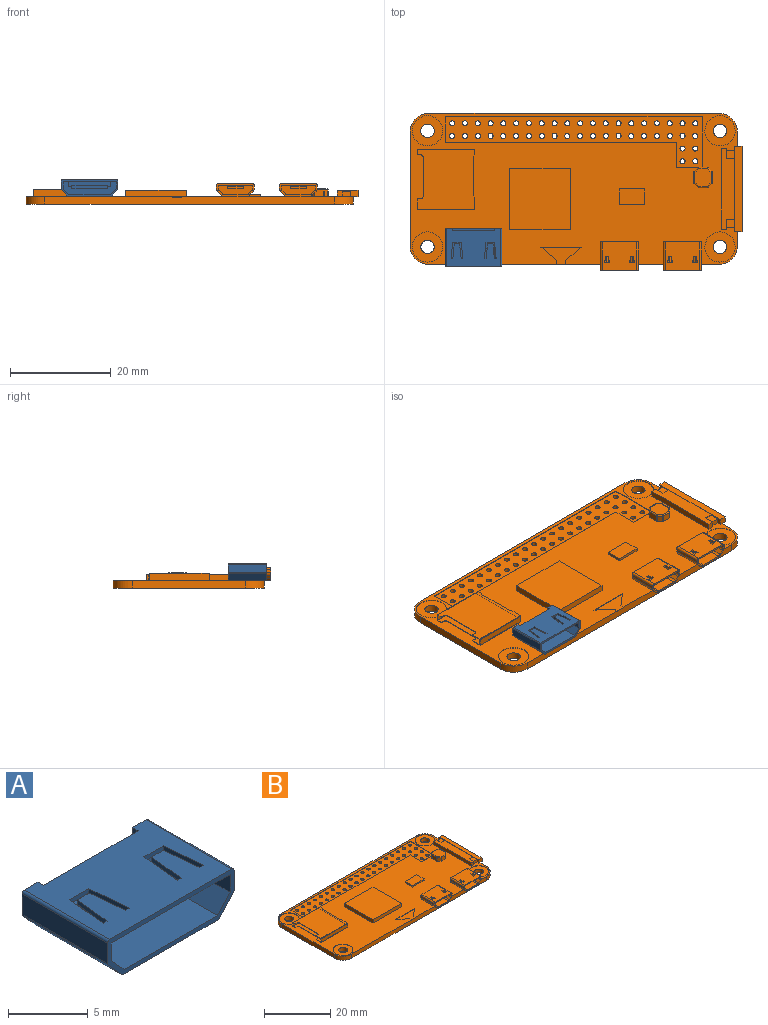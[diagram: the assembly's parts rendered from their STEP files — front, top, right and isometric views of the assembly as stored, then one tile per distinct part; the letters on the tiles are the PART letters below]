
ASSEMBLY  parts=2 mates=1
PART A: 46 faces, bbox 11.3x7.6x3.3 mm
  f0: plane 10.55x2.6mm, normal (0,-1,0), area 22.2mm2, adj f15,f16,f17,f18,f19,f20,f21,f22
  f1: plane 7.6x1.57mm, normal (-1,0,0), area 12mm2, adj f7,f8,f11,f13
  f2: plane 10.85x7.6mm, normal (0,0,1), area 72.9mm2, adj f7,f8,f13,f14,f26,f27,f28,f29
  f3: plane 7.6x1.57mm, normal (1,0,0), area 12mm2, adj f7,f8,f12,f14
  f4: plane 7.6x1.33mm, normal (0.74,0,-0.67), area 13.7mm2, adj f7,f8,f9,f12
  f5: plane 8.42x7.6mm, normal (0,0,-1), area 64mm2, adj f7,f8,f9,f10
  f6: plane 7.6x1.33mm, normal (-0.74,0,-0.67), area 13.7mm2, adj f7,f8,f10,f11
  f7: plane 11.25x3.3mm, normal (0,1,0), area 23.4mm2, adj f1,f2,f3,f4,f5,f6,f9,f10
  f8: plane 11.25x3.3mm, normal (0,-1,0), area 9.1mm2, adj f1,f2,f3,f4,f5,f6,f9,f10
  f9: cylinder r=0.2mm len=7.6mm, axis (0,-1,0), area 1.3mm2, adj f4,f5,f7,f8
  f10: cylinder r=0.2mm len=7.6mm, axis (0,-1,0), area 1.3mm2, adj f5,f6,f7,f8
  f11: cylinder r=0.2mm len=7.6mm, axis (0,-1,0), area 1.1mm2, adj f1,f6,f7,f8
  f12: cylinder r=0.2mm len=7.6mm, axis (0,-1,0), area 1.1mm2, adj f3,f4,f7,f8
  f13: cylinder r=0.2mm len=7.6mm, axis (0,-1,0), area 2.4mm2, adj f1,f2,f7,f8
  f14: cylinder r=0.2mm len=7.6mm, axis (0,-1,0), area 2.4mm2, adj f2,f3,f7,f8
  f15: plane 10.55x7mm, normal (0,0,-1), area 68.5mm2, adj f0,f8,f16,f20,f26,f27,f28,f29
  f16: plane 7x1.36mm, normal (-1,0,0), area 9.5mm2, adj f0,f8,f15,f17
  f17: plane 7x1.24mm, normal (-0.74,0,0.67), area 11.7mm2, adj f0,f8,f16,f18
  f18: plane 8.29x7mm, normal (0,0,1), area 58mm2, adj f0,f8,f17,f19
  f19: plane 7x1.24mm, normal (0.74,0,0.67), area 11.7mm2, adj f0,f8,f18,f20
  f20: plane 7x1.36mm, normal (1,0,0), area 9.5mm2, adj f0,f8,f15,f19
  f21: plane 3.5x0.55mm, normal (-1,0,0), area 1.9mm2, adj f0,f22,f24,f25
  f22: plane 7x3.5mm, normal (0,0,-1), area 24.5mm2, adj f0,f21,f23,f25
  f23: plane 3.5x0.55mm, normal (1,0,0), area 1.9mm2, adj f0,f22,f24,f25
  f24: plane 7x3.5mm, normal (0,0,1), area 24.5mm2, adj f0,f21,f23,f25
  f25: plane 7x0.55mm, normal (0,-1,0), area 3.8mm2, adj f21,f22,f23,f24
  f26: plane 3.3x0.35mm, normal (-1,-0.1,0), area 1.2mm2, adj f2,f15,f27,f33
  f27: plane 1.7x0.35mm, normal (0,-1,0), area 0.6mm2, adj f2,f15,f26,f28
  f28: plane 3.3x0.35mm, normal (1,-0.1,0), area 1.2mm2, adj f2,f15,f27,f29
  f29: plane 0.35x0.35mm, normal (0,1,0), area 0.1mm2, adj f2,f15,f28,f30
  f30: plane 2.95x0.35mm, normal (-1,0.1,0), area 1mm2, adj f2,f15,f29,f31
  f31: plane 1.07x0.35mm, normal (0,1,0), area 0.4mm2, adj f2,f15,f30,f32
  f32: plane 2.95x0.35mm, normal (1,0.1,0), area 1mm2, adj f2,f15,f31,f33
  f33: plane 0.35x0.35mm, normal (0,1,0), area 0.1mm2, adj f2,f15,f26,f32
  f34: plane 1.7x0.35mm, normal (0,-1,0), area 0.6mm2, adj f2,f15,f35,f41
  f35: plane 3.3x0.35mm, normal (1,-0.1,0), area 1.2mm2, adj f2,f15,f34,f36
  f36: plane 0.35x0.35mm, normal (0,1,0), area 0.1mm2, adj f2,f15,f35,f37
  f37: plane 2.95x0.35mm, normal (-1,0.1,0), area 1mm2, adj f2,f15,f36,f38
  f38: plane 1.07x0.35mm, normal (0,1,0), area 0.4mm2, adj f2,f15,f37,f39
  f39: plane 2.95x0.35mm, normal (1,0.1,0), area 1mm2, adj f2,f15,f38,f40
  f40: plane 0.35x0.35mm, normal (0,1,0), area 0.1mm2, adj f2,f15,f39,f41
  f41: plane 3.3x0.35mm, normal (-1,-0.1,0), area 1.2mm2, adj f2,f15,f34,f40
  f42: plane 1.4x0.5mm, normal (-1,0,0), area 0.7mm2, adj f2,f7,f44,f45
  f43: plane 1.4x0.5mm, normal (1,0,0), area 0.7mm2, adj f2,f7,f44,f45
  f44: plane 8.4x0.5mm, normal (0,0,1), area 4.2mm2, adj f7,f42,f43,f45
  f45: plane 8.4x1.4mm, normal (0,1,0), area 11.8mm2, adj f2,f42,f43,f44
PART B: 270 faces, bbox 65.9x31.3x4.1 mm
  f0: cylinder r=3mm len=6mm, axis (0,0,1), area 1.9mm2, adj f52,f91
  f1: cylinder r=3mm len=6mm, axis (0,0,1), area 1.9mm2, adj f52,f90
  f2: cylinder r=3mm len=6mm, axis (0,0,1), area 1.9mm2, adj f52,f89
  f3: cylinder r=3mm len=6mm, axis (0,0,1), area 1.9mm2, adj f52,f81
  f4: cylinder r=1.32mm len=2.65mm, axis (0,0,1), area 11.7mm2, adj f80,f81
  f5: cylinder r=0.5mm len=1.4mm, axis (0,0,1), area 4.4mm2, adj f80,f82
  f6: cylinder r=0.5mm len=1.4mm, axis (0,0,1), area 4.4mm2, adj f80,f82
  f7: cylinder r=0.5mm len=1.4mm, axis (0,0,1), area 4.4mm2, adj f80,f82
  f8: cylinder r=0.5mm len=1.4mm, axis (0,0,1), area 4.4mm2, adj f80,f82
  f9: cylinder r=0.5mm len=1.4mm, axis (0,0,1), area 4.4mm2, adj f80,f82
  f10: cylinder r=0.5mm len=1.4mm, axis (0,0,1), area 4.4mm2, adj f80,f82
  f11: cylinder r=0.5mm len=1.4mm, axis (0,0,1), area 4.4mm2, adj f80,f82
  f12: cylinder r=0.5mm len=1.4mm, axis (0,0,1), area 4.4mm2, adj f80,f82
  f13: cylinder r=1.32mm len=2.65mm, axis (0,0,1), area 11.7mm2, adj f80,f89
  f14: cylinder r=1.32mm len=2.65mm, axis (0,0,1), area 11.7mm2, adj f80,f90
  f15: cylinder r=1.32mm len=2.65mm, axis (0,0,1), area 11.7mm2, adj f80,f91
  f16: cylinder r=0.5mm len=1.4mm, axis (0,0,1), area 4.4mm2, adj f80,f82
  f17: cylinder r=0.5mm len=1.4mm, axis (0,0,1), area 4.4mm2, adj f80,f82
  f18: cylinder r=0.5mm len=1.4mm, axis (0,0,1), area 4.4mm2, adj f80,f82
  f19: cylinder r=0.5mm len=1.4mm, axis (0,0,1), area 4.4mm2, adj f80,f82
  f20: cylinder r=0.5mm len=1.4mm, axis (0,0,1), area 4.4mm2, adj f80,f82
  f21: cylinder r=0.5mm len=1.4mm, axis (0,0,1), area 4.4mm2, adj f80,f82
  f22: cylinder r=0.5mm len=1.4mm, axis (0,0,1), area 4.4mm2, adj f80,f82
  f23: cylinder r=0.5mm len=1.4mm, axis (0,0,1), area 4.4mm2, adj f80,f82
  f24: cylinder r=0.5mm len=1.4mm, axis (0,0,1), area 4.4mm2, adj f80,f82
  f25: cylinder r=0.5mm len=1.4mm, axis (0,0,1), area 4.4mm2, adj f80,f82
  f26: cylinder r=0.5mm len=1.4mm, axis (0,0,1), area 4.4mm2, adj f80,f82
  f27: cylinder r=0.5mm len=1.4mm, axis (0,0,1), area 4.4mm2, adj f80,f82
  f28: cylinder r=0.5mm len=1.4mm, axis (0,0,1), area 4.4mm2, adj f80,f82
  f29: cylinder r=0.5mm len=1.4mm, axis (0,0,1), area 4.4mm2, adj f80,f82
  f30: cylinder r=0.5mm len=1.4mm, axis (0,0,1), area 4.4mm2, adj f80,f82
  f31: cylinder r=0.5mm len=1.4mm, axis (0,0,1), area 4.4mm2, adj f80,f82
  f32: cylinder r=0.5mm len=1.4mm, axis (0,0,1), area 4.4mm2, adj f80,f82
  f33: cylinder r=0.5mm len=1.4mm, axis (0,0,1), area 4.4mm2, adj f80,f82
  f34: cylinder r=0.5mm len=1.4mm, axis (0,0,1), area 4.4mm2, adj f80,f82
  f35: cylinder r=0.5mm len=1.4mm, axis (0,0,1), area 4.4mm2, adj f80,f82
  f36: cylinder r=0.5mm len=1.4mm, axis (0,0,1), area 4.4mm2, adj f80,f82
  f37: cylinder r=0.5mm len=1.4mm, axis (0,0,1), area 4.4mm2, adj f80,f82
  f38: cylinder r=0.5mm len=1.4mm, axis (0,0,1), area 4.4mm2, adj f80,f82
  f39: cylinder r=0.5mm len=1.4mm, axis (0,0,1), area 4.4mm2, adj f80,f82
  f40: cylinder r=0.5mm len=1.4mm, axis (0,0,1), area 4.4mm2, adj f80,f82
  f41: cylinder r=0.5mm len=1.4mm, axis (0,0,1), area 4.4mm2, adj f80,f82
  f42: cylinder r=0.5mm len=1.4mm, axis (0,0,1), area 4.4mm2, adj f80,f82
  f43: cylinder r=0.5mm len=1.4mm, axis (0,0,1), area 4.4mm2, adj f80,f82
  f44: cylinder r=0.5mm len=1.4mm, axis (0,0,1), area 4.4mm2, adj f80,f82
  f45: cylinder r=0.5mm len=1.4mm, axis (0,0,1), area 4.4mm2, adj f80,f82
  f46: cylinder r=0.5mm len=1.4mm, axis (0,0,1), area 4.4mm2, adj f80,f82
  f47: cylinder r=0.5mm len=1.4mm, axis (0,0,1), area 4.4mm2, adj f80,f82
  f48: cylinder r=0.5mm len=1.4mm, axis (0,0,1), area 4.4mm2, adj f80,f82
  f49: cylinder r=0.5mm len=1.4mm, axis (0,0,1), area 4.4mm2, adj f80,f82
  f50: cylinder r=0.5mm len=1.4mm, axis (0,0,1), area 4.4mm2, adj f80,f82
  f51: cylinder r=0.5mm len=1.4mm, axis (0,0,1), area 4.4mm2, adj f80,f82
  f52: plane 65x30mm, normal (0,0,1), area 1137.8mm2, adj f0,f1,f2,f3,f53,f54,f55,f60
  f53: plane 17x1.2mm, normal (-1,0,0), area 2.7mm2, adj f52,f56,f212,f213,f214,f221,f222,f227
  f54: plane 2x1.19mm, normal (1,0,0), area 0.7mm2, adj f52,f221,f222,f223,f229,f230
  f55: plane 2x1.19mm, normal (1,0,0), area 0.7mm2, adj f52,f56,f221,f225,f227,f228
  f56: plane 1.6x0.19mm, normal (0,1,0), area 0.3mm2, adj f53,f55,f221,f228
  f57: plane 11.9x0.5mm, normal (0,0,1), area 6mm2, adj f77,f216,f218,f226
  f58: plane 6.91x1.96mm, normal (0,-1,0), area 11.2mm2, adj f158,f159,f160,f161,f162,f163,f164,f165
  f59: plane 6.91x1.96mm, normal (0,-1,0), area 11.2mm2, adj f146,f147,f148,f149,f150,f151,f152,f153
  f60: plane 1.45x1.1mm, normal (-1,0,0), area 0.3mm2, adj f52,f61,f62,f109,f110,f111,f113,f114
  f61: plane 0.65x0.1mm, normal (0,-1,0), area 0.1mm2, adj f52,f60,f63,f114
  f62: plane 0.65x0.1mm, normal (0,-1,0), area 0.1mm2, adj f60,f64,f110,f116
  f63: cylinder r=0.5mm len=0.5mm, axis (0,0,-1), area 0.1mm2, adj f52,f61,f65,f114
  f64: cylinder r=0.5mm len=0.5mm, axis (0,0,-1), area 0.1mm2, adj f62,f66,f110,f116
  f65: plane 7.75x0.1mm, normal (-1,0,0), area 0.8mm2, adj f52,f63,f67,f114
  f66: plane 7.75x0.1mm, normal (-1,0,0), area 0.8mm2, adj f64,f68,f110,f116
  f67: cylinder r=0.5mm len=0.5mm, axis (0,0,-1), area 0.1mm2, adj f52,f65,f69,f114
  f68: cylinder r=0.5mm len=0.5mm, axis (0,0,-1), area 0.1mm2, adj f66,f70,f110,f116
  f69: plane 0.65x0.1mm, normal (0,1,0), area 0.1mm2, adj f52,f67,f71,f114
  f70: plane 0.65x0.1mm, normal (0,1,0), area 0.1mm2, adj f68,f71,f110,f116
  f71: plane 2.15x1.45mm, normal (-1,0,0), area 0.6mm2, adj f52,f69,f70,f103,f110,f112,f114,f115
  f72: cylinder r=3.75mm len=3.75mm, axis (0,0,-1), area 8.8mm2, adj f52,f73,f79,f80
  f73: plane 22.5x1.5mm, normal (-1,0,0), area 33.8mm2, adj f52,f72,f74,f80
  f74: cylinder r=3.75mm len=3.75mm, axis (0,0,-1), area 8.8mm2, adj f52,f73,f75,f80
  f75: plane 57.5x1.5mm, normal (0,-1,0), area 86.1mm2, adj f52,f74,f76,f80,f95,f96,f97,f118
  f76: cylinder r=3.75mm len=3.75mm, axis (0,0,-1), area 8.8mm2, adj f52,f75,f77,f80
  f77: plane 22.5x1.5mm, normal (1,0,0), area 33.8mm2, adj f52,f57,f76,f78,f80,f215,f219
  f78: cylinder r=3.75mm len=3.75mm, axis (0,0,-1), area 8.8mm2, adj f52,f77,f79,f80
  f79: plane 57.5x1.5mm, normal (0,1,0), area 86.3mm2, adj f52,f72,f78,f80
  f80: plane 65x30mm, normal (0,0,-1), area 1881.3mm2, adj f4,f5,f6,f7,f8,f9,f10,f11
  f81: plane 6x6mm, normal (0,0,1), area 22.8mm2, adj f3,f4
  f82: plane 51x10.1mm, normal (0,0,1), area 251mm2, adj f5,f6,f7,f8,f9,f10,f11,f12
  f83: plane 5.1x0.1mm, normal (1,0,0), area 0.5mm2, adj f52,f82,f84,f88
  f84: plane 51x0.1mm, normal (0,-1,0), area 5.1mm2, adj f52,f82,f83,f85
  f85: plane 10.1x0.1mm, normal (-1,0,0), area 1mm2, adj f52,f82,f84,f86,f231
  f86: plane 5.1x0.1mm, normal (0,1,0), area 0.5mm2, adj f52,f82,f85,f87,f231
  f87: plane 5x0.1mm, normal (1,0,0), area 0.5mm2, adj f52,f82,f86,f88
  f88: plane 45.9x0.1mm, normal (0,1,0), area 4.6mm2, adj f52,f82,f83,f87
  f89: plane 6x6mm, normal (0,0,1), area 22.8mm2, adj f2,f13
  f90: plane 6x6mm, normal (0,0,1), area 22.8mm2, adj f1,f14
  f91: plane 6x6mm, normal (0,0,1), area 22.8mm2, adj f0,f15
  f92: plane 3.08x2.65mm, normal (0.65,0.76,0), area 0.4mm2, adj f52,f93,f96,f97
  f93: plane 8x0.1mm, normal (0,-1,0), area 0.8mm2, adj f52,f92,f94,f97
  f94: plane 3.08x2.65mm, normal (-0.65,0.76,0), area 0.4mm2, adj f52,f93,f95,f97
  f95: plane 0.8x0.1mm, normal (-1,0,0), area 0.1mm2, adj f52,f75,f94,f97
  f96: plane 0.8x0.1mm, normal (1,0,0), area 0.1mm2, adj f52,f75,f92,f97
  f97: plane 8x3.45mm, normal (0,0,1), area 14.5mm2, adj f75,f92,f93,f94,f95,f96
  f98: plane 12x1.25mm, normal (1,0,0), area 15mm2, adj f52,f99,f101,f102
  f99: plane 12x1.25mm, normal (0,1,0), area 15mm2, adj f52,f98,f100,f102
  f100: plane 12x1.25mm, normal (-1,0,0), area 15mm2, adj f52,f99,f101,f102
  f101: plane 12x1.25mm, normal (0,-1,0), area 15mm2, adj f52,f98,f100,f102
  f102: plane 12x12mm, normal (0,0,1), area 144mm2, adj f98,f99,f100,f101
  f103: plane 11.4x1.35mm, normal (0,-1,0), area 15.4mm2, adj f52,f71,f104,f112
  f104: plane 2.5x1.45mm, normal (1,0,0), area 3.6mm2, adj f52,f103,f105,f110,f112
  f105: plane 1.45x0.25mm, normal (0.71,0.71,0), area 0.5mm2, adj f52,f104,f106,f110
  f106: plane 7.9x1.45mm, normal (1,0,0), area 11.5mm2, adj f52,f105,f107,f110
  f107: plane 1.45x0.25mm, normal (0.71,-0.71,0), area 0.5mm2, adj f52,f106,f108,f110
  f108: plane 1.45x1.1mm, normal (1,0,0), area 1.6mm2, adj f52,f107,f109,f110,f111
  f109: plane 11.4x1.35mm, normal (0,1,0), area 15.4mm2, adj f52,f60,f108,f111
  f110: plane 11.8x11.4mm, normal (0,0,1), area 122.5mm2, adj f60,f62,f64,f66,f68,f70,f71,f104
  f111: cylinder r=0.1mm len=11.4mm, axis (-1,0,0), area 1.8mm2, adj f60,f108,f109,f110
  f112: cylinder r=0.1mm len=11.4mm, axis (1,0,0), area 1.8mm2, adj f71,f103,f104,f110
  f113: plane 10.65x1.25mm, normal (0,-1,0), area 13.3mm2, adj f60,f114,f116,f117
  f114: plane 11.8x10.65mm, normal (0,0,1), area 115.7mm2, adj f60,f61,f63,f65,f67,f69,f71,f113
  f115: plane 10.65x1.25mm, normal (0,1,0), area 13.3mm2, adj f71,f114,f116,f117
  f116: plane 11.8x10.65mm, normal (0,0,-1), area 115.7mm2, adj f60,f62,f64,f66,f68,f70,f71,f113
  f117: plane 11.8x1.25mm, normal (-1,0,0), area 14.7mm2, adj f113,f114,f115,f116
  f118: plane 4.3x1.25mm, normal (0,0,-1), area 5.4mm2, adj f75,f119,f120,f131
  f119: cylinder r=1mm len=5.75mm, axis (0,-1,0), area 4.6mm2, adj f52,f118,f129,f130,f131
  f120: cylinder r=1mm len=5.75mm, axis (0,-1,0), area 4.6mm2, adj f52,f118,f121,f130,f131
  f121: plane 5.75x0.65mm, normal (-0.72,0,-0.69), area 5.2mm2, adj f120,f122,f130,f131
  f122: cylinder r=1mm len=5.75mm, axis (0,-1,0), area 4.4mm2, adj f121,f123,f130,f131
  f123: plane 5.75x0.55mm, normal (-1,0,0), area 3.1mm2, adj f122,f124,f130,f131
  f124: cylinder r=0.4mm len=5.75mm, axis (0,-1,0), area 3.6mm2, adj f123,f125,f130,f131
  f125: plane 6.75x5.75mm, normal (0,0,1), area 36.8mm2, adj f124,f126,f130,f131,f188,f189,f190,f191
  f126: cylinder r=0.4mm len=5.75mm, axis (0,-1,0), area 3.6mm2, adj f125,f127,f130,f131
  f127: plane 5.75x0.55mm, normal (1,0,0), area 3.1mm2, adj f126,f128,f130,f131
  f128: cylinder r=1mm len=5.75mm, axis (0,-1,0), area 4.4mm2, adj f127,f129,f130,f131
  f129: plane 5.75x0.65mm, normal (0.72,0,-0.69), area 5.2mm2, adj f119,f128,f130,f131
  f130: plane 7.55x2.6mm, normal (0,1,0), area 18mm2, adj f52,f119,f120,f121,f122,f123,f124,f125
  f131: plane 7.55x2.6mm, normal (0,-1,0), area 5.6mm2, adj f118,f119,f120,f121,f122,f123,f124,f125
  f132: plane 4.3x1.25mm, normal (0,0,-1), area 5.4mm2, adj f75,f137,f138,f145
  f133: cylinder r=0.4mm len=5.75mm, axis (0,-1,0), area 3.6mm2, adj f134,f143,f144,f145
  f134: plane 5.75x0.55mm, normal (1,0,0), area 3.1mm2, adj f133,f135,f144,f145
  f135: cylinder r=1mm len=5.75mm, axis (0,-1,0), area 4.4mm2, adj f134,f136,f144,f145
  f136: plane 5.75x0.65mm, normal (0.72,0,-0.69), area 5.2mm2, adj f135,f137,f144,f145
  f137: cylinder r=1mm len=5.75mm, axis (0,-1,0), area 4.6mm2, adj f52,f132,f136,f144,f145
  f138: cylinder r=1mm len=5.75mm, axis (0,-1,0), area 4.6mm2, adj f52,f132,f139,f144,f145
  f139: plane 5.75x0.65mm, normal (-0.72,0,-0.69), area 5.2mm2, adj f138,f140,f144,f145
  f140: cylinder r=1mm len=5.75mm, axis (0,-1,0), area 4.4mm2, adj f139,f141,f144,f145
  f141: plane 5.75x0.55mm, normal (-1,0,0), area 3.1mm2, adj f140,f142,f144,f145
  f142: cylinder r=0.4mm len=5.75mm, axis (0,-1,0), area 3.6mm2, adj f141,f143,f144,f145
  f143: plane 6.75x5.75mm, normal (0,0,1), area 36.8mm2, adj f133,f142,f144,f145,f180,f181,f182,f183
  f144: plane 7.55x2.6mm, normal (0,1,0), area 18mm2, adj f52,f133,f134,f135,f136,f137,f138,f139
  f145: plane 7.55x2.6mm, normal (0,-1,0), area 5.6mm2, adj f132,f133,f134,f135,f136,f137,f138,f139
  f146: cylinder r=0.08mm len=5.25mm, axis (0,-1,0), area 0.7mm2, adj f59,f145,f147,f157
  f147: plane 5.25x0.55mm, normal (-1,0,0), area 2.9mm2, adj f59,f145,f146,f148
  f148: cylinder r=0.68mm len=5.25mm, axis (0,-1,0), area 2.7mm2, adj f59,f145,f147,f149
  f149: plane 5.25x0.65mm, normal (-0.72,0,0.69), area 4.7mm2, adj f59,f145,f148,f150
  f150: cylinder r=0.68mm len=5.25mm, axis (0,-1,0), area 2.9mm2, adj f59,f145,f149,f151
  f151: plane 5.25x4.3mm, normal (0,0,1), area 22.6mm2, adj f59,f145,f150,f152
  f152: cylinder r=0.68mm len=5.25mm, axis (0,-1,0), area 2.9mm2, adj f59,f145,f151,f153
  f153: plane 5.25x0.65mm, normal (0.72,0,0.69), area 4.7mm2, adj f59,f145,f152,f154
  f154: cylinder r=0.68mm len=5.25mm, axis (0,-1,0), area 2.7mm2, adj f59,f145,f153,f155
  f155: plane 5.25x0.55mm, normal (1,0,0), area 2.9mm2, adj f59,f145,f154,f156
  f156: cylinder r=0.08mm len=5.25mm, axis (0,-1,0), area 0.7mm2, adj f59,f145,f155,f157
  f157: plane 6.75x5.25mm, normal (0,0,-1), area 33.4mm2, adj f59,f145,f146,f156,f180,f181,f182,f183
  f158: cylinder r=0.68mm len=5.25mm, axis (0,-1,0), area 2.9mm2, adj f58,f131,f159,f169
  f159: plane 5.25x4.3mm, normal (0,0,1), area 22.6mm2, adj f58,f131,f158,f160
  f160: cylinder r=0.68mm len=5.25mm, axis (0,-1,0), area 2.9mm2, adj f58,f131,f159,f161
  f161: plane 5.25x0.65mm, normal (0.72,0,0.69), area 4.7mm2, adj f58,f131,f160,f162
  f162: cylinder r=0.68mm len=5.25mm, axis (0,-1,0), area 2.7mm2, adj f58,f131,f161,f163
  f163: plane 5.25x0.55mm, normal (1,0,0), area 2.9mm2, adj f58,f131,f162,f164
  f164: cylinder r=0.08mm len=5.25mm, axis (0,-1,0), area 0.7mm2, adj f58,f131,f163,f165
  f165: plane 6.75x5.25mm, normal (0,0,-1), area 33.4mm2, adj f58,f131,f164,f166,f188,f189,f190,f191
  f166: cylinder r=0.08mm len=5.25mm, axis (0,-1,0), area 0.7mm2, adj f58,f131,f165,f167
  f167: plane 5.25x0.55mm, normal (-1,0,0), area 2.9mm2, adj f58,f131,f166,f168
  f168: cylinder r=0.68mm len=5.25mm, axis (0,-1,0), area 2.7mm2, adj f58,f131,f167,f169
  f169: plane 5.25x0.65mm, normal (-0.72,0,0.69), area 4.7mm2, adj f58,f131,f158,f168
  f170: plane 3.5x0.4mm, normal (1,0,0), area 1.4mm2, adj f59,f171,f173,f174
  f171: plane 3.5x3.15mm, normal (0,0,1), area 11mm2, adj f59,f170,f172,f174
  f172: plane 3.5x0.4mm, normal (-1,0,0), area 1.4mm2, adj f59,f171,f173,f174
  f173: plane 3.5x3.15mm, normal (0,0,-1), area 11mm2, adj f59,f170,f172,f174
  f174: plane 3.15x0.4mm, normal (0,-1,0), area 1.3mm2, adj f170,f171,f172,f173
  f175: plane 3.5x0.4mm, normal (1,0,0), area 1.4mm2, adj f58,f176,f178,f179
  f176: plane 3.5x3.15mm, normal (0,0,1), area 11mm2, adj f58,f175,f177,f179
  f177: plane 3.5x0.4mm, normal (-1,0,0), area 1.4mm2, adj f58,f176,f178,f179
  f178: plane 3.5x3.15mm, normal (0,0,-1), area 11mm2, adj f58,f175,f177,f179
  f179: plane 3.15x0.4mm, normal (0,-1,0), area 1.3mm2, adj f175,f176,f177,f178
  f180: plane 0.45x0.32mm, normal (-1,0,0), area 0.1mm2, adj f143,f157,f181,f187
  f181: plane 1.05x0.32mm, normal (0,1,0), area 0.3mm2, adj f143,f157,f180,f182
  f182: plane 0.45x0.32mm, normal (1,0,0), area 0.1mm2, adj f143,f157,f181,f183
  f183: plane 0.32x0.23mm, normal (0,-1,0), area 0.1mm2, adj f143,f157,f182,f184
  f184: plane 0.9x0.32mm, normal (1,0,0), area 0.3mm2, adj f143,f157,f183,f185
  f185: plane 0.6x0.32mm, normal (0,-1,0), area 0.2mm2, adj f143,f157,f184,f186
  f186: plane 0.9x0.32mm, normal (-1,0,0), area 0.3mm2, adj f143,f157,f185,f187
  f187: plane 0.32x0.23mm, normal (0,-1,0), area 0.1mm2, adj f143,f157,f180,f186
  f188: plane 0.6x0.32mm, normal (0,-1,0), area 0.2mm2, adj f125,f165,f189,f195
  f189: plane 0.9x0.32mm, normal (-1,0,0), area 0.3mm2, adj f125,f165,f188,f190
  f190: plane 0.32x0.23mm, normal (0,-1,0), area 0.1mm2, adj f125,f165,f189,f191
  f191: plane 0.45x0.32mm, normal (-1,0,0), area 0.1mm2, adj f125,f165,f190,f192
  f192: plane 1.05x0.32mm, normal (0,1,0), area 0.3mm2, adj f125,f165,f191,f193
  f193: plane 0.45x0.32mm, normal (1,0,0), area 0.1mm2, adj f125,f165,f192,f194
  f194: plane 0.32x0.23mm, normal (0,-1,0), area 0.1mm2, adj f125,f165,f193,f195
  f195: plane 0.9x0.32mm, normal (1,0,0), area 0.3mm2, adj f125,f165,f188,f194
  f196: plane 0.9x0.32mm, normal (-1,0,0), area 0.3mm2, adj f125,f165,f197,f203
  f197: plane 0.32x0.23mm, normal (0,-1,0), area 0.1mm2, adj f125,f165,f196,f198
  f198: plane 0.45x0.32mm, normal (-1,0,0), area 0.1mm2, adj f125,f165,f197,f199
  f199: plane 1.05x0.32mm, normal (0,1,0), area 0.3mm2, adj f125,f165,f198,f200
  f200: plane 0.45x0.32mm, normal (1,0,0), area 0.1mm2, adj f125,f165,f199,f201
  f201: plane 0.32x0.23mm, normal (0,-1,0), area 0.1mm2, adj f125,f165,f200,f202
  f202: plane 0.9x0.32mm, normal (1,0,0), area 0.3mm2, adj f125,f165,f201,f203
  f203: plane 0.6x0.32mm, normal (0,-1,0), area 0.2mm2, adj f125,f165,f196,f202
  f204: plane 0.6x0.32mm, normal (0,-1,0), area 0.2mm2, adj f143,f157,f205,f211
  f205: plane 0.9x0.32mm, normal (-1,0,0), area 0.3mm2, adj f143,f157,f204,f206
  f206: plane 0.32x0.23mm, normal (0,-1,0), area 0.1mm2, adj f143,f157,f205,f207
  f207: plane 0.45x0.32mm, normal (-1,0,0), area 0.1mm2, adj f143,f157,f206,f208
  f208: plane 1.05x0.32mm, normal (0,1,0), area 0.3mm2, adj f143,f157,f207,f209
  f209: plane 0.45x0.32mm, normal (1,0,0), area 0.1mm2, adj f143,f157,f208,f210
  f210: plane 0.32x0.23mm, normal (0,-1,0), area 0.1mm2, adj f143,f157,f209,f211
  f211: plane 0.9x0.32mm, normal (1,0,0), area 0.3mm2, adj f143,f157,f204,f210
  f212: plane 1.4x1.2mm, normal (0,-1,0), area 1.7mm2, adj f52,f53,f213,f219,f220
  f213: plane 17x1.4mm, normal (0,0,1), area 23.8mm2, adj f53,f212,f214,f220
  f214: plane 1.4x1.2mm, normal (0,1,0), area 1.7mm2, adj f52,f53,f213,f215,f220
  f215: plane 2.55x0.9mm, normal (0,0,-1), area 2.3mm2, adj f77,f214,f216,f220
  f216: plane 1.4x0.65mm, normal (0,-1,0), area 0.9mm2, adj f57,f215,f217,f220,f226
  f217: plane 11.9x1.4mm, normal (0,0,-1), area 16.7mm2, adj f216,f218,f220,f226
  f218: plane 1.4x0.65mm, normal (0,1,0), area 0.9mm2, adj f57,f217,f219,f220,f226
  f219: plane 2.55x0.9mm, normal (0,0,-1), area 2.3mm2, adj f77,f212,f218,f220
  f220: plane 17x1.2mm, normal (1,0,0), area 12.7mm2, adj f212,f213,f214,f215,f216,f217,f218,f219
  f221: plane 16x2.7mm, normal (0,0,1), area 36.8mm2, adj f53,f54,f55,f56,f222,f223,f224,f225
  f222: plane 1.6x0.19mm, normal (0,-1,0), area 0.3mm2, adj f53,f54,f221,f230
  f223: plane 1.19x1.1mm, normal (0,-1,0), area 1.3mm2, adj f52,f54,f221,f224
  f224: plane 16x1.19mm, normal (-1,0,0), area 19mm2, adj f52,f221,f223,f225
  f225: plane 1.19x1.1mm, normal (0,1,0), area 1.3mm2, adj f52,f55,f221,f224
  f226: plane 11.9x0.65mm, normal (1,0,0), area 7.7mm2, adj f57,f216,f217,f218
  f227: plane 1.6x1mm, normal (0,1,0), area 1.6mm2, adj f52,f53,f55,f228
  f228: plane 1.7x1.6mm, normal (0,0,1), area 2.7mm2, adj f53,f55,f56,f227
  f229: plane 1.6x1mm, normal (0,-1,0), area 1.6mm2, adj f52,f53,f54,f230
  f230: plane 1.7x1.6mm, normal (0,0,1), area 2.7mm2, adj f53,f54,f222,f229
  f231: plane 0.8x0.05mm, normal (0,0,-1), area 0mm2, adj f85,f86,f235,f260
  f232: plane 2.03x1.3mm, normal (-1,0,0), area 2.6mm2, adj f52,f248,f253,f254
  f233: plane 1.68x1.3mm, normal (0,-1,0), area 2.2mm2, adj f52,f246,f251,f252
  f234: plane 2.03x1.3mm, normal (1,0,0), area 2.6mm2, adj f52,f257,f263,f264
  f235: plane 1.68x1.3mm, normal (0,1,0), area 2.2mm2, adj f52,f231,f260,f265,f266
  f236: plane 3.6x3.25mm, normal (0,0,1), area 10.5mm2, adj f247,f252,f253,f258,f259,f264,f265,f269
  f237: plane 1.3x0.78mm, normal (-0.71,0.71,0), area 1.4mm2, adj f52,f254,f259,f260
  f238: plane 1.3x0.78mm, normal (0.71,0.71,0), area 1.4mm2, adj f52,f263,f266,f269
  f239: plane 1.3x0.78mm, normal (0.71,-0.71,0), area 1.4mm2, adj f52,f251,f257,f258
  f240: plane 1.3x0.78mm, normal (-0.71,-0.71,0), area 1.4mm2, adj f52,f246,f247,f248
  f241: plane 3.15x0.5mm, normal (-1,0,0), area 1.6mm2, adj f52,f242,f244,f245
  f242: plane 5x0.5mm, normal (0,-1,0), area 2.5mm2, adj f52,f241,f243,f245
  f243: plane 3.15x0.5mm, normal (1,0,0), area 1.6mm2, adj f52,f242,f244,f245
  f244: plane 5x0.5mm, normal (0,1,0), area 2.5mm2, adj f52,f241,f243,f245
  f245: plane 5x3.15mm, normal (0,0,1), area 15.7mm2, adj f241,f242,f243,f244
  f246: cylinder r=0.2mm len=1.3mm, axis (0,0,-1), area 0.2mm2, adj f52,f233,f240,f249
  f247: cylinder r=0.2mm len=0.92mm, axis (-0.71,0.71,0), area 0.3mm2, adj f236,f240,f249,f250
  f248: cylinder r=0.2mm len=1.3mm, axis (0,0,1), area 0.2mm2, adj f52,f232,f240,f250
  f249: sphere r=0.2mm, area 0mm2, adj f246,f247,f252
  f250: sphere r=0.2mm, area 0mm2, adj f247,f248,f253
  f251: cylinder r=0.2mm len=1.3mm, axis (0,0,1), area 0.2mm2, adj f52,f233,f239,f255
  f252: cylinder r=0.2mm len=1.68mm, axis (-1,0,0), area 0.5mm2, adj f233,f236,f249,f255
  f253: cylinder r=0.2mm len=2.03mm, axis (0,1,0), area 0.6mm2, adj f232,f236,f250,f256
  f254: cylinder r=0.2mm len=1.3mm, axis (0,0,-1), area 0.2mm2, adj f52,f232,f237,f256
  f255: sphere r=0.2mm, area 0mm2, adj f251,f252,f258
  f256: sphere r=0.2mm, area 0mm2, adj f253,f254,f259
  f257: cylinder r=0.2mm len=1.3mm, axis (0,0,-1), area 0.2mm2, adj f52,f234,f239,f261
  f258: cylinder r=0.2mm len=0.92mm, axis (-0.71,-0.71,0), area 0.3mm2, adj f236,f239,f255,f261
  f259: cylinder r=0.2mm len=0.92mm, axis (0.71,0.71,0), area 0.3mm2, adj f236,f237,f256,f262
  f260: cylinder r=0.2mm len=1.3mm, axis (0,0,1), area 0.2mm2, adj f52,f231,f235,f237,f262
  f261: sphere r=0.2mm, area 0mm2, adj f257,f258,f264
  f262: sphere r=0.2mm, area 0mm2, adj f259,f260,f265
  f263: cylinder r=0.2mm len=1.3mm, axis (0,0,1), area 0.2mm2, adj f52,f234,f238,f267
  f264: cylinder r=0.2mm len=2.03mm, axis (0,-1,0), area 0.6mm2, adj f234,f236,f261,f267
  f265: cylinder r=0.2mm len=1.68mm, axis (1,0,0), area 0.5mm2, adj f235,f236,f262,f268
  f266: cylinder r=0.2mm len=1.3mm, axis (0,0,-1), area 0.2mm2, adj f52,f235,f238,f268
  f267: sphere r=0.2mm, area 0mm2, adj f263,f264,f269
  f268: sphere r=0.2mm, area 0mm2, adj f265,f266,f269
  f269: cylinder r=0.2mm len=0.92mm, axis (0.71,-0.71,0), area 0.3mm2, adj f236,f238,f267,f268
PLACE A at identity
PLACE B at identity fixed
MATE fastened A.f5 <-> B.f52  axis (0,0,-1) through (-19.87,-11.6,1.5)mm
